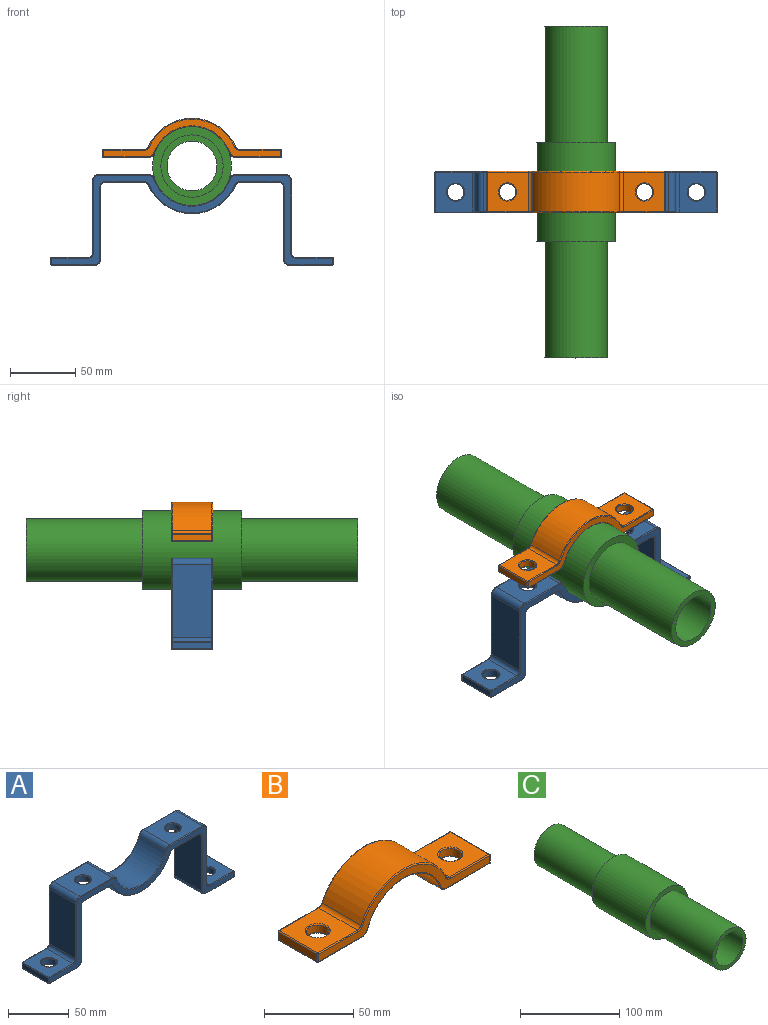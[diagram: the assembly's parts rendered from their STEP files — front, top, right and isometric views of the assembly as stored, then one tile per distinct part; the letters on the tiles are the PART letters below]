
ASSEMBLY  parts=3 mates=2
PART A: 108 faces, bbox 215.9x31.8x70.7 mm
  f0: plane 30.48x30.3mm, normal (0,0,-1), area 770.3mm2, adj f24,f29,f37,f71,f106
  f1: cylinder r=36.51mm len=66.93mm, axis (0,1,0), area 2580.3mm2, adj f24,f25,f59,f102
  f2: plane 30.48x30.3mm, normal (0,0,-1), area 770.3mm2, adj f25,f26,f35,f47,f98
  f3: plane 55.25x30.48mm, normal (-1,0,0), area 1683.9mm2, adj f18,f26,f52,f92
  f4: plane 32.39x30.48mm, normal (0,0,-1), area 860.4mm2, adj f18,f33,f65,f75,f83
  f5: plane 30.48x5.08mm, normal (1,0,0), area 154.8mm2, adj f63,f64,f74,f75
  f6: plane 30.48x27.94mm, normal (0,0,1), area 698.3mm2, adj f27,f34,f51,f62,f63
  f7: plane 55.25x30.48mm, normal (1,0,0), area 1683.9mm2, adj f19,f27,f42,f50
  f8: plane 37.78x30.48mm, normal (0,0,1), area 998.3mm2, adj f19,f20,f36,f41,f49
  f9: cylinder r=30.16mm len=57.06mm, axis (0,1,0), area 2280.9mm2, adj f20,f21,f48,f61
  f10: plane 37.78x30.48mm, normal (0,0,1), area 998.3mm2, adj f21,f22,f38,f60,f73
  f11: plane 55.25x30.48mm, normal (-1,0,0), area 1683.9mm2, adj f22,f28,f72,f82
  f12: plane 30.48x27.94mm, normal (0,0,1), area 698.3mm2, adj f28,f39,f81,f90,f91
  f13: plane 30.48x5.08mm, normal (-1,0,0), area 154.8mm2, adj f89,f90,f96,f97
  f14: plane 32.39x30.48mm, normal (0,0,-1), area 860.4mm2, adj f23,f30,f88,f96,f101
  f15: plane 55.25x30.48mm, normal (1,0,0), area 1683.9mm2, adj f23,f29,f80,f105
  f16: plane 214.63x68.58mm, normal (0,-1,0), area 1838.7mm2, adj f44,f49,f50,f55,f56,f61,f62,f68
  f17: plane 214.63x68.58mm, normal (0,1,0), area 1838.7mm2, adj f40,f41,f42,f43,f45,f46,f47,f48
  f18: cylinder r=5.08mm len=30.48mm, axis (0,1,0), area 243.2mm2, adj f3,f4,f58,f87
  f19: cylinder r=5.08mm len=30.48mm, axis (0,1,0), area 243.2mm2, adj f7,f8,f40,f44
  f20: cylinder r=5.08mm len=30.48mm, axis (0,1,0), area 192.1mm2, adj f8,f9,f43,f55
  f21: cylinder r=5.08mm len=30.48mm, axis (0,1,0), area 192.1mm2, adj f9,f10,f54,f68
  f22: cylinder r=5.08mm len=30.48mm, axis (0,-1,0), area 243.2mm2, adj f10,f11,f67,f78
  f23: cylinder r=5.08mm len=30.48mm, axis (0,1,0), area 243.2mm2, adj f14,f15,f84,f103
  f24: cylinder r=3.17mm len=30.48mm, axis (0,1,0), area 112.2mm2, adj f0,f1,f66,f104
  f25: cylinder r=3.17mm len=30.48mm, axis (0,1,0), area 112.2mm2, adj f1,f2,f53,f100
  f26: cylinder r=3.17mm len=30.48mm, axis (0,1,0), area 152mm2, adj f2,f3,f46,f95
  f27: cylinder r=3.17mm len=30.48mm, axis (0,-1,0), area 152mm2, adj f6,f7,f45,f56
  f28: cylinder r=3.17mm len=30.48mm, axis (0,-1,0), area 152mm2, adj f11,f12,f77,f86
  f29: cylinder r=3.17mm len=30.48mm, axis (0,-1,0), area 152mm2, adj f0,f15,f76,f107
  f30: cylinder r=6.35mm len=12.7mm, axis (0,0,1), area 228mm2, adj f14,f39
  f31: cylinder r=6.35mm len=12.7mm, axis (0,0,1), area 202.7mm2, adj f37,f38
  f32: cylinder r=6.35mm len=12.7mm, axis (0,0,1), area 202.7mm2, adj f35,f36
  f33: cylinder r=6.35mm len=12.7mm, axis (0,0,1), area 228mm2, adj f4,f34
  f34: torus R=6.99mm, axis (0,0,-1), area 41.2mm2, adj f6,f33
  f35: torus R=6.99mm, axis (0,0,-1), area 41.2mm2, adj f2,f32
  f36: torus R=6.99mm, axis (0,0,-1), area 41.2mm2, adj f8,f32
  f37: torus R=6.99mm, axis (0,0,-1), area 41.2mm2, adj f0,f31
  f38: torus R=6.99mm, axis (0,0,-1), area 41.2mm2, adj f10,f31
  f39: torus R=6.99mm, axis (0,0,1), area 41.2mm2, adj f12,f30
  f40: torus R=4.45mm, axis (0,-1,0), area 7.6mm2, adj f17,f19,f41,f42
  f41: cylinder r=0.64mm len=37.78mm, axis (-1,0,0), area 37.7mm2, adj f8,f17,f40,f43
  f42: cylinder r=0.64mm len=55.25mm, axis (0,0,1), area 55.1mm2, adj f7,f17,f40,f45
  f43: torus R=4.45mm, axis (0,-1,0), area 6mm2, adj f17,f20,f41,f48
  f44: torus R=4.45mm, axis (0,-1,0), area 7.6mm2, adj f16,f19,f49,f50
  f45: torus R=3.81mm, axis (0,-1,0), area 5.3mm2, adj f17,f27,f42,f51
  f46: torus R=3.81mm, axis (0,-1,0), area 5.3mm2, adj f17,f26,f47,f52
  f47: cylinder r=0.64mm len=30.3mm, axis (1,0,0), area 30.2mm2, adj f2,f17,f46,f53
  f48: torus R=30.8mm, axis (0,-1,0), area 75.2mm2, adj f9,f17,f43,f54
  f49: cylinder r=0.64mm len=37.78mm, axis (1,0,0), area 37.7mm2, adj f8,f16,f44,f55
  f50: cylinder r=0.64mm len=55.25mm, axis (0,0,-1), area 55.1mm2, adj f7,f16,f44,f56
  f51: cylinder r=0.64mm len=27.94mm, axis (-1,0,0), area 27.9mm2, adj f6,f17,f45,f57
  f52: cylinder r=0.64mm len=55.25mm, axis (0,0,-1), area 55.1mm2, adj f3,f17,f46,f58
  f53: torus R=3.81mm, axis (0,-1,0), area 3.9mm2, adj f17,f25,f47,f59
  f54: torus R=4.45mm, axis (0,-1,0), area 6mm2, adj f17,f21,f48,f60
  f55: torus R=4.45mm, axis (0,-1,0), area 6mm2, adj f16,f20,f49,f61
  f56: torus R=3.81mm, axis (0,-1,0), area 5.3mm2, adj f16,f27,f50,f62
  f57: sphere r=0.64mm, area 0.6mm2, adj f51,f63,f64
  f58: torus R=4.45mm, axis (0,-1,0), area 7.6mm2, adj f17,f18,f52,f65
  f59: torus R=35.88mm, axis (0,-1,0), area 83.9mm2, adj f1,f17,f53,f66
  f60: cylinder r=0.64mm len=37.78mm, axis (-1,0,0), area 37.7mm2, adj f10,f17,f54,f67
  f61: torus R=30.8mm, axis (0,-1,0), area 75.2mm2, adj f9,f16,f55,f68
  f62: cylinder r=0.64mm len=27.94mm, axis (1,0,0), area 27.9mm2, adj f6,f16,f56,f69
  f63: cylinder r=0.64mm len=30.48mm, axis (0,1,0), area 30.4mm2, adj f5,f6,f57,f69
  f64: cylinder r=0.64mm len=5.08mm, axis (0,0,1), area 5.1mm2, adj f5,f17,f57,f70
  f65: cylinder r=0.64mm len=32.39mm, axis (1,0,0), area 32.3mm2, adj f4,f17,f58,f70
  f66: torus R=3.81mm, axis (0,-1,0), area 3.9mm2, adj f17,f24,f59,f71
  f67: torus R=4.45mm, axis (0,-1,0), area 7.6mm2, adj f17,f22,f60,f72
  f68: torus R=4.45mm, axis (0,-1,0), area 6mm2, adj f16,f21,f61,f73
  f69: sphere r=0.64mm, area 0.6mm2, adj f62,f63,f74
  f70: sphere r=0.64mm, area 0.6mm2, adj f64,f65,f75
  f71: cylinder r=0.64mm len=30.3mm, axis (1,0,0), area 30.2mm2, adj f0,f17,f66,f76
  f72: cylinder r=0.64mm len=55.25mm, axis (0,0,-1), area 55.1mm2, adj f11,f17,f67,f77
  f73: cylinder r=0.64mm len=37.78mm, axis (1,0,0), area 37.7mm2, adj f10,f16,f68,f78
  f74: cylinder r=0.64mm len=5.08mm, axis (0,0,-1), area 5.1mm2, adj f5,f16,f69,f79
  f75: cylinder r=0.64mm len=30.48mm, axis (0,1,0), area 30.4mm2, adj f4,f5,f70,f79
  f76: torus R=3.81mm, axis (0,-1,0), area 5.3mm2, adj f17,f29,f71,f80
  f77: torus R=3.81mm, axis (0,-1,0), area 5.3mm2, adj f17,f28,f72,f81
  f78: torus R=4.45mm, axis (0,-1,0), area 7.6mm2, adj f16,f22,f73,f82
  f79: sphere r=0.64mm, area 0.6mm2, adj f74,f75,f83
  f80: cylinder r=0.64mm len=55.25mm, axis (0,0,1), area 55.1mm2, adj f15,f17,f76,f84
  f81: cylinder r=0.64mm len=27.94mm, axis (-1,0,0), area 27.9mm2, adj f12,f17,f77,f85
  f82: cylinder r=0.64mm len=55.25mm, axis (0,0,1), area 55.1mm2, adj f11,f16,f78,f86
  f83: cylinder r=0.64mm len=32.39mm, axis (-1,0,0), area 32.3mm2, adj f4,f16,f79,f87
  f84: torus R=4.45mm, axis (0,-1,0), area 7.6mm2, adj f17,f23,f80,f88
  f85: sphere r=0.64mm, area 0.6mm2, adj f81,f89,f90
  f86: torus R=3.81mm, axis (0,-1,0), area 5.3mm2, adj f16,f28,f82,f91
  f87: torus R=4.45mm, axis (0,-1,0), area 7.6mm2, adj f16,f18,f83,f92
  f88: cylinder r=0.64mm len=32.39mm, axis (1,0,0), area 32.3mm2, adj f14,f17,f84,f93
  f89: cylinder r=0.64mm len=5.08mm, axis (0,0,-1), area 5.1mm2, adj f13,f17,f85,f93
  f90: cylinder r=0.64mm len=30.48mm, axis (0,1,0), area 30.4mm2, adj f12,f13,f85,f94
  f91: cylinder r=0.64mm len=27.94mm, axis (1,0,0), area 27.9mm2, adj f12,f16,f86,f94
  f92: cylinder r=0.64mm len=55.25mm, axis (0,0,1), area 55.1mm2, adj f3,f16,f87,f95
  f93: sphere r=0.64mm, area 0.6mm2, adj f88,f89,f96
  f94: sphere r=0.64mm, area 0.6mm2, adj f90,f91,f97
  f95: torus R=3.81mm, axis (0,-1,0), area 5.3mm2, adj f16,f26,f92,f98
  f96: cylinder r=0.64mm len=30.48mm, axis (0,1,0), area 30.4mm2, adj f13,f14,f93,f99
  f97: cylinder r=0.64mm len=5.08mm, axis (0,0,1), area 5.1mm2, adj f13,f16,f94,f99
  f98: cylinder r=0.64mm len=30.3mm, axis (-1,0,0), area 30.2mm2, adj f2,f16,f95,f100
  f99: sphere r=0.64mm, area 0.6mm2, adj f96,f97,f101
  f100: torus R=3.81mm, axis (0,-1,0), area 3.9mm2, adj f16,f25,f98,f102
  f101: cylinder r=0.64mm len=32.39mm, axis (-1,0,0), area 32.3mm2, adj f14,f16,f99,f103
  f102: torus R=35.88mm, axis (0,-1,0), area 83.9mm2, adj f1,f16,f100,f104
  f103: torus R=4.45mm, axis (0,-1,0), area 7.6mm2, adj f16,f23,f101,f105
  f104: torus R=3.81mm, axis (0,-1,0), area 3.9mm2, adj f16,f24,f102,f106
  f105: cylinder r=0.64mm len=55.25mm, axis (0,0,-1), area 55.1mm2, adj f15,f16,f103,f107
  f106: cylinder r=0.64mm len=30.3mm, axis (-1,0,0), area 30.2mm2, adj f0,f16,f104,f107
  f107: torus R=3.81mm, axis (0,-1,0), area 5.3mm2, adj f16,f29,f105,f106
PART B: 52 faces, bbox 136.5x31.8x33.6 mm
  f0: cylinder r=36.51mm len=66.93mm, axis (0,1,0), area 2580.3mm2, adj f12,f13,f28,f48
  f1: plane 31.25x30.48mm, normal (0,0,1), area 799.3mm2, adj f12,f16,f34,f40,f44
  f2: plane 30.48x5.08mm, normal (-1,0,0), area 154.8mm2, adj f32,f33,f39,f40
  f3: plane 34.29x30.48mm, normal (0,0,-1), area 891.9mm2, adj f10,f17,f27,f31,f32
  f4: cylinder r=30.16mm len=57.06mm, axis (0,1,0), area 2280.9mm2, adj f10,f11,f23,f38
  f5: plane 34.29x30.48mm, normal (0,0,-1), area 891.9mm2, adj f11,f18,f20,f43,f51
  f6: plane 30.48x5.08mm, normal (1,0,0), area 154.8mm2, adj f22,f45,f50,f51
  f7: plane 31.25x30.48mm, normal (0,0,1), area 799.3mm2, adj f13,f19,f24,f47,f50
  f8: plane 135.26x28.89mm, normal (0,-1,0), area 794.8mm2, adj f31,f35,f38,f39,f41,f43,f44,f45
  f9: plane 135.26x28.89mm, normal (0,1,0), area 794.8mm2, adj f20,f21,f22,f23,f24,f25,f26,f27
  f10: cylinder r=5.08mm len=30.48mm, axis (0,1,0), area 192.1mm2, adj f3,f4,f25,f35
  f11: cylinder r=5.08mm len=30.48mm, axis (0,1,0), area 192.1mm2, adj f4,f5,f21,f41
  f12: cylinder r=3.17mm len=30.48mm, axis (0,1,0), area 112.2mm2, adj f0,f1,f30,f46
  f13: cylinder r=3.17mm len=30.48mm, axis (0,1,0), area 112.2mm2, adj f0,f7,f26,f49
  f14: cylinder r=6.35mm len=12.7mm, axis (0,0,-1), area 202.7mm2, adj f18,f19
  f15: cylinder r=6.35mm len=12.7mm, axis (0,0,-1), area 202.7mm2, adj f16,f17
  f16: torus R=6.99mm, axis (0,0,-1), area 41.2mm2, adj f1,f15
  f17: torus R=6.99mm, axis (0,0,-1), area 41.2mm2, adj f3,f15
  f18: torus R=6.99mm, axis (0,0,-1), area 41.2mm2, adj f5,f14
  f19: torus R=6.99mm, axis (0,0,-1), area 41.2mm2, adj f7,f14
  f20: cylinder r=0.64mm len=34.74mm, axis (1,0,0), area 34.4mm2, adj f5,f9,f21,f22,f51
  f21: torus R=4.45mm, axis (0,-1,0), area 6mm2, adj f9,f11,f20,f23
  f22: cylinder r=0.64mm len=5.98mm, axis (0,0,1), area 5.5mm2, adj f6,f9,f20,f24,f50,f51
  f23: torus R=30.8mm, axis (0,-1,0), area 75.2mm2, adj f4,f9,f21,f25
  f24: cylinder r=0.64mm len=31.7mm, axis (-1,0,0), area 31.4mm2, adj f7,f9,f22,f26,f50
  f25: torus R=4.45mm, axis (0,-1,0), area 6mm2, adj f9,f10,f23,f27
  f26: torus R=3.81mm, axis (0,-1,0), area 3.9mm2, adj f9,f13,f24,f28
  f27: cylinder r=0.64mm len=34.29mm, axis (1,0,0), area 34.2mm2, adj f3,f9,f25,f29
  f28: torus R=35.88mm, axis (0,-1,0), area 83.9mm2, adj f0,f9,f26,f30
  f29: sphere r=0.64mm, area 0.6mm2, adj f27,f32,f33
  f30: torus R=3.81mm, axis (0,-1,0), area 3.9mm2, adj f9,f12,f28,f34
  f31: cylinder r=0.64mm len=34.29mm, axis (-1,0,0), area 34.2mm2, adj f3,f8,f35,f36
  f32: cylinder r=0.64mm len=30.48mm, axis (0,1,0), area 30.4mm2, adj f2,f3,f29,f36
  f33: cylinder r=0.64mm len=5.08mm, axis (0,0,-1), area 5.1mm2, adj f2,f9,f29,f37
  f34: cylinder r=0.64mm len=31.25mm, axis (-1,0,0), area 31.2mm2, adj f1,f9,f30,f37
  f35: torus R=4.45mm, axis (0,-1,0), area 6mm2, adj f8,f10,f31,f38
  f36: sphere r=0.64mm, area 0.6mm2, adj f31,f32,f39
  f37: sphere r=0.64mm, area 0.6mm2, adj f33,f34,f40
  f38: torus R=30.8mm, axis (0,-1,0), area 75.2mm2, adj f4,f8,f35,f41
  f39: cylinder r=0.64mm len=5.08mm, axis (0,0,1), area 5.1mm2, adj f2,f8,f36,f42
  f40: cylinder r=0.64mm len=30.48mm, axis (0,-1,0), area 30.4mm2, adj f1,f2,f37,f42
  f41: torus R=4.45mm, axis (0,-1,0), area 6mm2, adj f8,f11,f38,f43
  f42: sphere r=0.64mm, area 0.6mm2, adj f39,f40,f44
  f43: cylinder r=0.64mm len=34.74mm, axis (-1,0,0), area 34.4mm2, adj f5,f8,f41,f45,f51
  f44: cylinder r=0.64mm len=31.25mm, axis (1,0,0), area 31.2mm2, adj f1,f8,f42,f46
  f45: cylinder r=0.64mm len=5.98mm, axis (0,0,-1), area 5.5mm2, adj f6,f8,f43,f47,f50,f51
  f46: torus R=3.81mm, axis (0,-1,0), area 3.9mm2, adj f8,f12,f44,f48
  f47: cylinder r=0.64mm len=31.7mm, axis (1,0,0), area 31.4mm2, adj f7,f8,f45,f49,f50
  f48: torus R=35.88mm, axis (0,-1,0), area 83.9mm2, adj f0,f8,f46,f49
  f49: torus R=3.81mm, axis (0,-1,0), area 3.9mm2, adj f8,f13,f47,f48
  f50: cylinder r=0.64mm len=31.38mm, axis (0,1,0), area 30.9mm2, adj f6,f7,f22,f24,f45,f47
  f51: cylinder r=0.64mm len=31.38mm, axis (0,-1,0), area 30.9mm2, adj f5,f6,f20,f22,f43,f45
PART C: 8 faces, bbox 60.3x254x60.3 mm
  f0: cylinder r=30.16mm len=76.2mm, axis (0,1,0), area 14441.2mm2, adj f1,f2
  f1: plane 60.33x60.33mm, normal (0,-1,0), area 1076.8mm2, adj f0,f3
  f2: plane 60.33x60.33mm, normal (0,1,0), area 1076.8mm2, adj f0,f4
  f3: cylinder r=23.81mm len=88.9mm, axis (0,1,0), area 13301.1mm2, adj f1,f6
  f4: cylinder r=23.81mm len=88.9mm, axis (0,1,0), area 13301.1mm2, adj f2,f7
  f5: cylinder r=19.05mm len=254mm, axis (0,1,0), area 30402.4mm2, adj f6,f7
  f6: plane 47.63x47.63mm, normal (0,-1,0), area 641.3mm2, adj f3,f5
  f7: plane 47.63x47.63mm, normal (0,1,0), area 641.3mm2, adj f4,f5
PLACE A t=(-149.05,-131.5,22.9)mm
PLACE B t=(-149.05,-131.5,22.9)mm
PLACE C t=(-149.05,-131.5,22.9)mm
MATE fastened B.f0 <-> C.f0  axis (0,1,0) through (-149.05,-131.5,22.9)mm
MATE fastened C.f0 <-> A.f1  axis (0,1,0) through (-149.05,-131.5,22.9)mm
